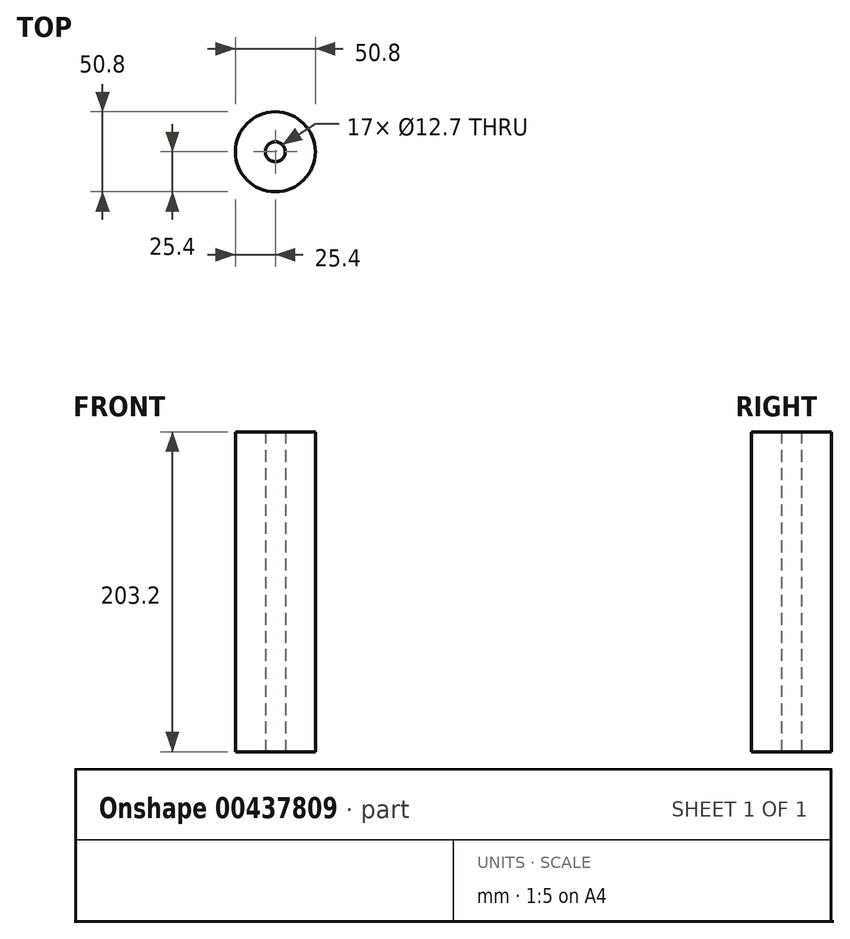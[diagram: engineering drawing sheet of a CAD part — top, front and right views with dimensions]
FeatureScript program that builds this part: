
annotation { "Feature Type Name" : "Feature", "Feature Type Description" : "" }
export const myFeature = defineFeature(function(context is Context, id is Id, definition is map)
    precondition{}
    {
        {
            var Q0;
            Q0=qCreatedBy(makeId("Top.planeOp"),FACE);
            var sketch = newSketch(context, id + "F0", { "sketchPlane" : qUnion([Q0])});
            skCircle(sketch, "E0", {"center": v(0, 0) * mm, "radius": 25.4 * mm});
            skCircle(sketch, "E1.0", {"center": v(0, 0) * mm, "radius": 6.35 * mm});
            skSolve(sketch);
        }
        {
            var Q0;
            Q0 = qSketchRegion(id + "F0", true);
            extrude(context, id + "F1", {"entities" : qUnion([Q0]), "depth" : 101.6 * mm, "hasSecondDirection" : true, "secondDirectionOppositeDirection" : true, "secondDirectionDepth" : 101.6 * mm});
        }
    });
